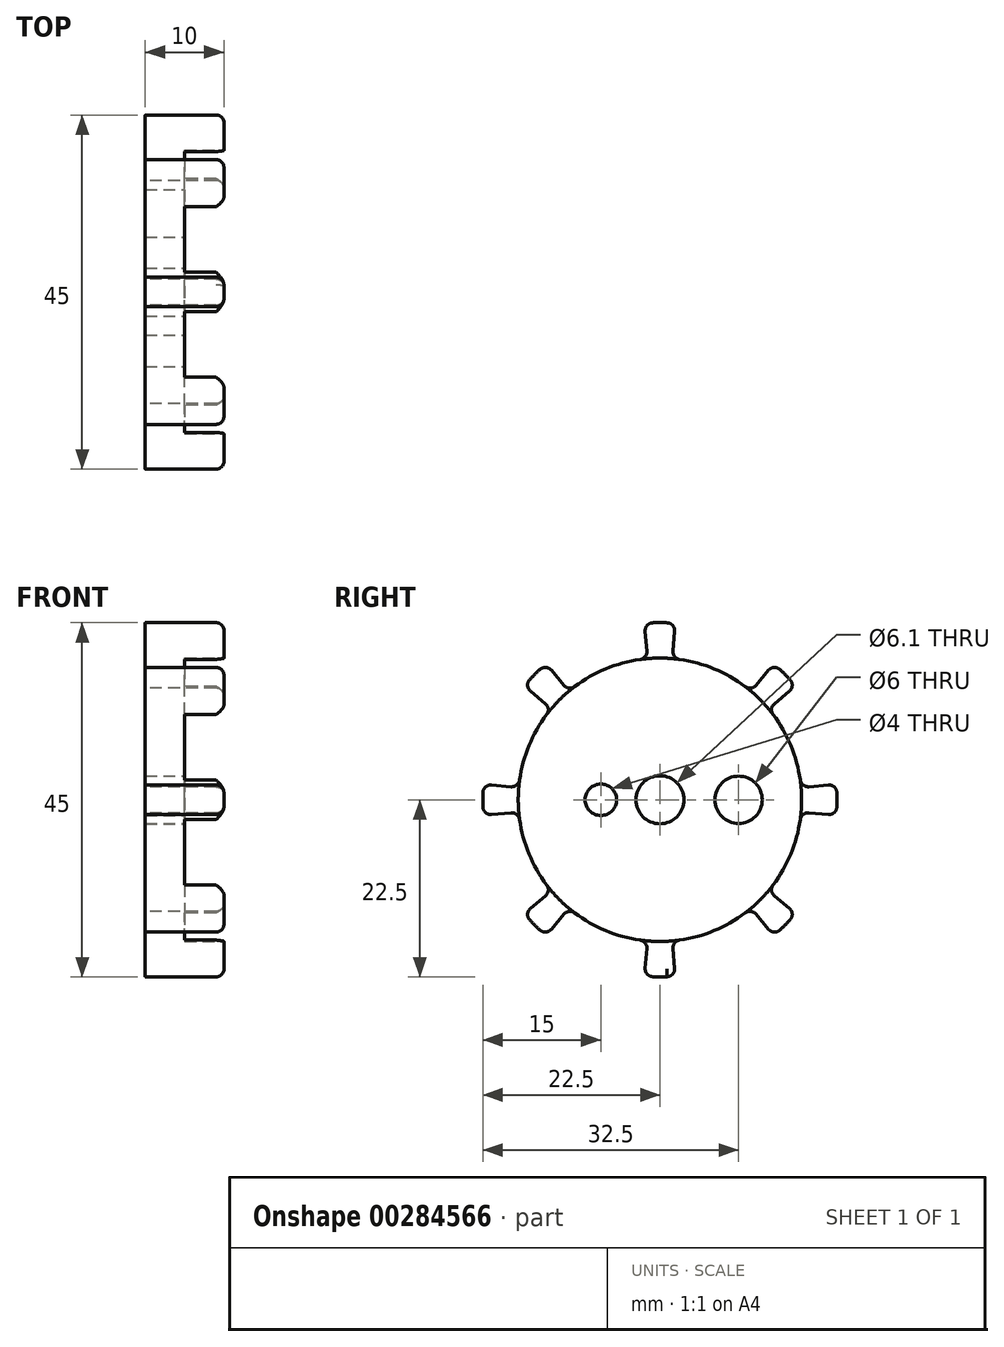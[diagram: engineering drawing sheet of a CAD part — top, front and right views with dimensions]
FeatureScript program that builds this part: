
annotation { "Feature Type Name" : "Feature", "Feature Type Description" : "" }
export const myFeature = defineFeature(function(context is Context, id is Id, definition is map)
    precondition{}
    {
        {
            var Q0;
            Q0=qCreatedBy(makeId("Right.planeOp"),FACE);
            var sketch = newSketch(context, id + "F0", { "sketchPlane" : qUnion([Q0])});
            skArc(sketch, "E0", {"start": v(0.92, 22.48) * mm, "mid": v(0, 22.5) * mm, "end": v(-0.92, 22.48) * mm});
            skArc(sketch, "E1", {"start": v(-2.51, 17.82) * mm, "mid": v(-6.89, 16.63) * mm, "end": v(-10.83, 14.38) * mm});
            skLineSegment(sketch, "E2", {"start": v(0, 22.5) * mm, "end": v(0, 0) * mm, "construction": true});
            skLineSegment(sketch, "E3", {"start": v(1.57, 17.93) * mm, "end": v(0, 0) * mm, "construction": true});
            skLineSegment(sketch, "E4", {"start": v(-1.57, 17.93) * mm, "end": v(0, 0) * mm, "construction": true});
            skLineSegment(sketch, "E5", {"start": v(-1.87, 21.4) * mm, "end": v(-1.65, 18.9) * mm});
            skLineSegment(sketch, "E6", {"start": v(1.87, 21.4) * mm, "end": v(1.65, 18.9) * mm});
            skLineSegment(sketch, "E7.1.0", {"start": v(-16.45, 13.8) * mm, "end": v(-14.53, 12.2) * mm});
            skArc(sketch, "E7.1.1", {"start": v(-15.25, 16.54) * mm, "mid": v(-15.9, 15.9) * mm, "end": v(-16.54, 15.25) * mm});
            skLineSegment(sketch, "E7.1.2", {"start": v(-13.8, 16.45) * mm, "end": v(-12.2, 14.53) * mm});
            skLineSegment(sketch, "E7.2.0", {"start": v(-21.4, -1.87) * mm, "end": v(-18.9, -1.65) * mm});
            skArc(sketch, "E7.2.1", {"start": v(-22.48, 0.92) * mm, "mid": v(-22.5, 0) * mm, "end": v(-22.48, -0.92) * mm});
            skLineSegment(sketch, "E7.2.2", {"start": v(-21.4, 1.87) * mm, "end": v(-18.9, 1.65) * mm});
            skLineSegment(sketch, "E7.3.0", {"start": v(-13.8, -16.45) * mm, "end": v(-12.2, -14.53) * mm});
            skArc(sketch, "E7.3.1", {"start": v(-16.54, -15.25) * mm, "mid": v(-15.9, -15.9) * mm, "end": v(-15.25, -16.54) * mm});
            skLineSegment(sketch, "E7.3.2", {"start": v(-16.45, -13.8) * mm, "end": v(-14.53, -12.2) * mm});
            skLineSegment(sketch, "E7.4.0", {"start": v(1.87, -21.4) * mm, "end": v(1.65, -18.9) * mm});
            skArc(sketch, "E7.4.1", {"start": v(-0.92, -22.48) * mm, "mid": v(0, -22.5) * mm, "end": v(0.92, -22.48) * mm});
            skLineSegment(sketch, "E7.4.2", {"start": v(-1.87, -21.4) * mm, "end": v(-1.65, -18.9) * mm});
            skLineSegment(sketch, "E7.5.0", {"start": v(16.45, -13.8) * mm, "end": v(14.53, -12.2) * mm});
            skArc(sketch, "E7.5.1", {"start": v(15.25, -16.54) * mm, "mid": v(15.9, -15.9) * mm, "end": v(16.54, -15.25) * mm});
            skLineSegment(sketch, "E7.5.2", {"start": v(13.8, -16.45) * mm, "end": v(12.2, -14.53) * mm});
            skLineSegment(sketch, "E7.6.0", {"start": v(21.4, 1.87) * mm, "end": v(18.9, 1.65) * mm});
            skArc(sketch, "E7.6.1", {"start": v(22.48, -0.92) * mm, "mid": v(22.5, 0) * mm, "end": v(22.48, 0.92) * mm});
            skLineSegment(sketch, "E7.6.2", {"start": v(21.4, -1.87) * mm, "end": v(18.9, -1.65) * mm});
            skLineSegment(sketch, "E7.7.0", {"start": v(13.8, 16.45) * mm, "end": v(12.2, 14.53) * mm});
            skArc(sketch, "E7.7.1", {"start": v(16.54, 15.25) * mm, "mid": v(15.9, 15.9) * mm, "end": v(15.25, 16.54) * mm});
            skLineSegment(sketch, "E7.7.2", {"start": v(16.45, 13.8) * mm, "end": v(14.53, 12.2) * mm});
            skArc(sketch, "E8.trimOffspring", {"start": v(-14.38, 10.83) * mm, "mid": v(-16.63, 6.89) * mm, "end": v(-17.82, 2.51) * mm});
            skArc(sketch, "E9.trimOffspring", {"start": v(-17.82, -2.51) * mm, "mid": v(-16.63, -6.89) * mm, "end": v(-14.38, -10.83) * mm});
            skArc(sketch, "E10.trimOffspring", {"start": v(-10.83, -14.38) * mm, "mid": v(-6.89, -16.63) * mm, "end": v(-2.51, -17.82) * mm});
            skArc(sketch, "E11.trimOffspring", {"start": v(2.51, -17.82) * mm, "mid": v(6.89, -16.63) * mm, "end": v(10.83, -14.38) * mm});
            skArc(sketch, "E12.trimOffspring", {"start": v(14.38, -10.83) * mm, "mid": v(16.63, -6.89) * mm, "end": v(17.82, -2.51) * mm});
            skArc(sketch, "E13.trimOffspring", {"start": v(17.82, 2.51) * mm, "mid": v(16.63, 6.89) * mm, "end": v(14.38, 10.83) * mm});
            skArc(sketch, "E14.trimOffspring", {"start": v(10.83, 14.38) * mm, "mid": v(6.89, 16.63) * mm, "end": v(2.51, 17.82) * mm});
            skPoint(sketch, "E15.visualSharp", {"position": v(-1.57, 17.93) * mm});
            skArc(sketch, "E15.filletArc", {"start": v(-2.51, 17.82) * mm, "mid": v(-1.87, 18.2) * mm, "end": v(-1.65, 18.9) * mm});
            skPoint(sketch, "E16.visualSharp", {"position": v(1.57, 17.93) * mm});
            skArc(sketch, "E16.filletArc", {"start": v(1.65, 18.9) * mm, "mid": v(1.87, 18.2) * mm, "end": v(2.51, 17.82) * mm});
            skPoint(sketch, "E17.visualSharp", {"position": v(1.96, 22.41) * mm});
            skArc(sketch, "E17.filletArc", {"start": v(1.87, 21.4) * mm, "mid": v(1.63, 22.14) * mm, "end": v(0.92, 22.48) * mm});
            skPoint(sketch, "E18.visualSharp", {"position": v(-1.96, 22.41) * mm});
            skArc(sketch, "E18.filletArc", {"start": v(-0.92, 22.48) * mm, "mid": v(-1.63, 22.14) * mm, "end": v(-1.87, 21.4) * mm});
            skPoint(sketch, "E19.visualSharp", {"position": v(14.46, 17.24) * mm});
            skArc(sketch, "E19.filletArc", {"start": v(15.25, 16.54) * mm, "mid": v(14.5, 16.8) * mm, "end": v(13.8, 16.45) * mm});
            skPoint(sketch, "E20.visualSharp", {"position": v(11.57, 13.79) * mm});
            skArc(sketch, "E20.filletArc", {"start": v(10.83, 14.38) * mm, "mid": v(11.54, 14.18) * mm, "end": v(12.2, 14.53) * mm});
            skPoint(sketch, "E21.visualSharp", {"position": v(17.24, 14.46) * mm});
            skArc(sketch, "E21.filletArc", {"start": v(16.45, 13.8) * mm, "mid": v(16.8, 14.5) * mm, "end": v(16.54, 15.25) * mm});
            skPoint(sketch, "E22.visualSharp", {"position": v(13.79, 11.57) * mm});
            skArc(sketch, "E22.filletArc", {"start": v(14.53, 12.2) * mm, "mid": v(14.18, 11.54) * mm, "end": v(14.38, 10.83) * mm});
            skPoint(sketch, "E23.visualSharp", {"position": v(17.93, 1.57) * mm});
            skArc(sketch, "E23.filletArc", {"start": v(17.82, 2.51) * mm, "mid": v(18.2, 1.87) * mm, "end": v(18.9, 1.65) * mm});
            skPoint(sketch, "E24.visualSharp", {"position": v(22.41, 1.96) * mm});
            skArc(sketch, "E24.filletArc", {"start": v(22.48, 0.92) * mm, "mid": v(22.14, 1.63) * mm, "end": v(21.4, 1.87) * mm});
            skPoint(sketch, "E25.visualSharp", {"position": v(22.41, -1.96) * mm});
            skArc(sketch, "E25.filletArc", {"start": v(21.4, -1.87) * mm, "mid": v(22.14, -1.63) * mm, "end": v(22.48, -0.92) * mm});
            skPoint(sketch, "E26.visualSharp", {"position": v(17.93, -1.57) * mm});
            skArc(sketch, "E26.filletArc", {"start": v(18.9, -1.65) * mm, "mid": v(18.2, -1.87) * mm, "end": v(17.82, -2.51) * mm});
            skPoint(sketch, "E27.visualSharp", {"position": v(-11.57, 13.79) * mm});
            skArc(sketch, "E27.filletArc", {"start": v(-12.2, 14.53) * mm, "mid": v(-11.54, 14.18) * mm, "end": v(-10.83, 14.38) * mm});
            skPoint(sketch, "E28.visualSharp", {"position": v(-14.46, 17.24) * mm});
            skArc(sketch, "E28.filletArc", {"start": v(-13.8, 16.45) * mm, "mid": v(-14.5, 16.8) * mm, "end": v(-15.25, 16.54) * mm});
            skPoint(sketch, "E29.visualSharp", {"position": v(-17.24, 14.46) * mm});
            skArc(sketch, "E29.filletArc", {"start": v(-16.54, 15.25) * mm, "mid": v(-16.8, 14.5) * mm, "end": v(-16.45, 13.8) * mm});
            skPoint(sketch, "E30.visualSharp", {"position": v(-13.79, 11.57) * mm});
            skArc(sketch, "E30.filletArc", {"start": v(-14.38, 10.83) * mm, "mid": v(-14.18, 11.54) * mm, "end": v(-14.53, 12.2) * mm});
            skPoint(sketch, "E31.visualSharp", {"position": v(-17.93, 1.57) * mm});
            skArc(sketch, "E31.filletArc", {"start": v(-18.9, 1.65) * mm, "mid": v(-18.2, 1.87) * mm, "end": v(-17.82, 2.51) * mm});
            skPoint(sketch, "E32.visualSharp", {"position": v(-22.41, 1.96) * mm});
            skArc(sketch, "E32.filletArc", {"start": v(-21.4, 1.87) * mm, "mid": v(-22.14, 1.63) * mm, "end": v(-22.48, 0.92) * mm});
            skPoint(sketch, "E33.visualSharp", {"position": v(-22.41, -1.96) * mm});
            skArc(sketch, "E33.filletArc", {"start": v(-22.48, -0.92) * mm, "mid": v(-22.14, -1.63) * mm, "end": v(-21.4, -1.87) * mm});
            skPoint(sketch, "E34.visualSharp", {"position": v(-17.93, -1.57) * mm});
            skArc(sketch, "E34.filletArc", {"start": v(-17.82, -2.51) * mm, "mid": v(-18.2, -1.87) * mm, "end": v(-18.9, -1.65) * mm});
            skPoint(sketch, "E35.visualSharp", {"position": v(-13.79, -11.57) * mm});
            skArc(sketch, "E35.filletArc", {"start": v(-14.53, -12.2) * mm, "mid": v(-14.18, -11.54) * mm, "end": v(-14.38, -10.83) * mm});
            skPoint(sketch, "E36.visualSharp", {"position": v(-17.24, -14.46) * mm});
            skArc(sketch, "E36.filletArc", {"start": v(-16.45, -13.8) * mm, "mid": v(-16.8, -14.5) * mm, "end": v(-16.54, -15.25) * mm});
            skPoint(sketch, "E37.visualSharp", {"position": v(-14.46, -17.24) * mm});
            skArc(sketch, "E37.filletArc", {"start": v(-15.25, -16.54) * mm, "mid": v(-14.5, -16.8) * mm, "end": v(-13.8, -16.45) * mm});
            skPoint(sketch, "E38.visualSharp", {"position": v(-11.57, -13.79) * mm});
            skArc(sketch, "E38.filletArc", {"start": v(-10.83, -14.38) * mm, "mid": v(-11.54, -14.18) * mm, "end": v(-12.2, -14.53) * mm});
            skPoint(sketch, "E39.visualSharp", {"position": v(-1.57, -17.93) * mm});
            skArc(sketch, "E39.filletArc", {"start": v(-1.65, -18.9) * mm, "mid": v(-1.87, -18.2) * mm, "end": v(-2.51, -17.82) * mm});
            skPoint(sketch, "E40.visualSharp", {"position": v(-1.96, -22.41) * mm});
            skArc(sketch, "E40.filletArc", {"start": v(-1.87, -21.4) * mm, "mid": v(-1.63, -22.14) * mm, "end": v(-0.92, -22.48) * mm});
            skPoint(sketch, "E41.visualSharp", {"position": v(1.96, -22.41) * mm});
            skArc(sketch, "E41.filletArc", {"start": v(0.92, -22.48) * mm, "mid": v(1.63, -22.14) * mm, "end": v(1.87, -21.4) * mm});
            skPoint(sketch, "E42.visualSharp", {"position": v(1.57, -17.93) * mm});
            skArc(sketch, "E42.filletArc", {"start": v(2.51, -17.82) * mm, "mid": v(1.87, -18.2) * mm, "end": v(1.65, -18.9) * mm});
            skPoint(sketch, "E43.visualSharp", {"position": v(11.57, -13.79) * mm});
            skArc(sketch, "E43.filletArc", {"start": v(12.2, -14.53) * mm, "mid": v(11.54, -14.18) * mm, "end": v(10.83, -14.38) * mm});
            skPoint(sketch, "E44.visualSharp", {"position": v(14.46, -17.24) * mm});
            skArc(sketch, "E44.filletArc", {"start": v(13.8, -16.45) * mm, "mid": v(14.5, -16.8) * mm, "end": v(15.25, -16.54) * mm});
            skPoint(sketch, "E45.visualSharp", {"position": v(17.24, -14.46) * mm});
            skArc(sketch, "E45.filletArc", {"start": v(16.54, -15.25) * mm, "mid": v(16.8, -14.5) * mm, "end": v(16.45, -13.8) * mm});
            skPoint(sketch, "E46.visualSharp", {"position": v(13.79, -11.57) * mm});
            skArc(sketch, "E46.filletArc", {"start": v(14.38, -10.83) * mm, "mid": v(14.18, -11.54) * mm, "end": v(14.53, -12.2) * mm});
            skSolve(sketch);
        }
        {
            var Q0;
            Q0=qSketchRegion(id+"F0",true);
            extrude(context, id + "F1", {"entities" : qUnion([Q0]), "depth" : 10 * mm});
        }
        {
            var Q0;
            Q0=makeQuery(id+"F1.opExtrude","CAP_FACE",FACE,{"disambiguationData":[OSD([sQuery(id+"F0.wireOp",EDGE,"E0"),sQuery(id+"F0.wireOp",EDGE,"E1"),sQuery(id+"F0.wireOp",EDGE,"E5"),sQuery(id+"F0.wireOp",EDGE,"E6"),sQuery(id+"F0.wireOp",EDGE,"E7.1.0"),sQuery(id+"F0.wireOp",EDGE,"E7.1.1"),sQuery(id+"F0.wireOp",EDGE,"E7.1.2"),sQuery(id+"F0.wireOp",EDGE,"E7.2.0"),sQuery(id+"F0.wireOp",EDGE,"E7.2.1"),sQuery(id+"F0.wireOp",EDGE,"E7.2.2"),sQuery(id+"F0.wireOp",EDGE,"E7.3.0"),sQuery(id+"F0.wireOp",EDGE,"E7.3.1"),sQuery(id+"F0.wireOp",EDGE,"E7.3.2"),sQuery(id+"F0.wireOp",EDGE,"E7.4.0"),sQuery(id+"F0.wireOp",EDGE,"E7.4.1"),sQuery(id+"F0.wireOp",EDGE,"E7.4.2"),sQuery(id+"F0.wireOp",EDGE,"E7.5.0"),sQuery(id+"F0.wireOp",EDGE,"E7.5.1"),sQuery(id+"F0.wireOp",EDGE,"E7.5.2"),sQuery(id+"F0.wireOp",EDGE,"E7.6.0"),sQuery(id+"F0.wireOp",EDGE,"E7.6.1"),sQuery(id+"F0.wireOp",EDGE,"E7.6.2"),sQuery(id+"F0.wireOp",EDGE,"E7.7.0"),sQuery(id+"F0.wireOp",EDGE,"E7.7.1"),sQuery(id+"F0.wireOp",EDGE,"E7.7.2"),sQuery(id+"F0.wireOp",EDGE,"E8.trimOffspring"),sQuery(id+"F0.wireOp",EDGE,"E9.trimOffspring"),sQuery(id+"F0.wireOp",EDGE,"E10.trimOffspring"),sQuery(id+"F0.wireOp",EDGE,"E11.trimOffspring"),sQuery(id+"F0.wireOp",EDGE,"E12.trimOffspring"),sQuery(id+"F0.wireOp",EDGE,"E13.trimOffspring"),sQuery(id+"F0.wireOp",EDGE,"E14.trimOffspring")])],"isStart":false});
            var sketch = newSketch(context, id + "F2", { "sketchPlane" : qUnion([Q0])});
            skCircle(sketch, "E47", {"center": v(0, 0) * mm, "radius": 18 * mm});
            skSolve(sketch);
        }
        {
            var Q0;
            Q0=qSketchRegion(id+"F2",true);
            extrude(context, id + "F3", {"entities" : qUnion([Q0]), "operationType" : NewBodyOperationType.REMOVE, "oppositeDirection" : true, "depth" : 5 * mm});
        }
        {
            var Q0;
            Q0=makeQuery(id+"F3.boolean.opBoolean","COPY",FACE,{"derivedFrom":makeQuery(id+"F3.opExtrude","CAP_FACE",FACE,{"disambiguationData":[OSD([sQuery(id+"F2.wireOp",EDGE,"E47")])],"isStart":false})});
            var sketch = newSketch(context, id + "F4", { "sketchPlane" : qUnion([Q0])});
            skPoint(sketch, "E48", {"position": v(10, 0) * mm});
            skPoint(sketch, "E49", {"position": v(0, 0) * mm});
            skPoint(sketch, "E50", {"position": v(-7.5, 0) * mm});
            skSolve(sketch);
        }
        {
            var Q0;
            Q0=sQuery(id+"F4.wireOp",VERTEX,"E49");
            var Q1;
            Q1=makeQuery(id+"F1.opExtrude","SWEPT_BODY",BODY,{"disambiguationData":[OSD([sQuery(id+"F0.wireOp",EDGE,"E0"),sQuery(id+"F0.wireOp",EDGE,"E1"),sQuery(id+"F0.wireOp",EDGE,"E5"),sQuery(id+"F0.wireOp",EDGE,"E6"),sQuery(id+"F0.wireOp",EDGE,"E7.1.0"),sQuery(id+"F0.wireOp",EDGE,"E7.1.1"),sQuery(id+"F0.wireOp",EDGE,"E7.1.2"),sQuery(id+"F0.wireOp",EDGE,"E7.2.0"),sQuery(id+"F0.wireOp",EDGE,"E7.2.1"),sQuery(id+"F0.wireOp",EDGE,"E7.2.2"),sQuery(id+"F0.wireOp",EDGE,"E7.3.0"),sQuery(id+"F0.wireOp",EDGE,"E7.3.1"),sQuery(id+"F0.wireOp",EDGE,"E7.3.2"),sQuery(id+"F0.wireOp",EDGE,"E7.4.0"),sQuery(id+"F0.wireOp",EDGE,"E7.4.1"),sQuery(id+"F0.wireOp",EDGE,"E7.4.2"),sQuery(id+"F0.wireOp",EDGE,"E7.5.0"),sQuery(id+"F0.wireOp",EDGE,"E7.5.1"),sQuery(id+"F0.wireOp",EDGE,"E7.5.2"),sQuery(id+"F0.wireOp",EDGE,"E7.6.0"),sQuery(id+"F0.wireOp",EDGE,"E7.6.1"),sQuery(id+"F0.wireOp",EDGE,"E7.6.2"),sQuery(id+"F0.wireOp",EDGE,"E7.7.0"),sQuery(id+"F0.wireOp",EDGE,"E7.7.1"),sQuery(id+"F0.wireOp",EDGE,"E7.7.2"),sQuery(id+"F0.wireOp",EDGE,"E8.trimOffspring"),sQuery(id+"F0.wireOp",EDGE,"E9.trimOffspring"),sQuery(id+"F0.wireOp",EDGE,"E10.trimOffspring"),sQuery(id+"F0.wireOp",EDGE,"E11.trimOffspring"),sQuery(id+"F0.wireOp",EDGE,"E12.trimOffspring"),sQuery(id+"F0.wireOp",EDGE,"E13.trimOffspring"),sQuery(id+"F0.wireOp",EDGE,"E14.trimOffspring"),sQuery(id+"F0.wireOp",EDGE,"E15.filletArc"),sQuery(id+"F0.wireOp",EDGE,"E16.filletArc"),sQuery(id+"F0.wireOp",EDGE,"E17.filletArc"),sQuery(id+"F0.wireOp",EDGE,"E18.filletArc"),sQuery(id+"F0.wireOp",EDGE,"E19.filletArc"),sQuery(id+"F0.wireOp",EDGE,"E20.filletArc"),sQuery(id+"F0.wireOp",EDGE,"E21.filletArc"),sQuery(id+"F0.wireOp",EDGE,"E22.filletArc"),sQuery(id+"F0.wireOp",EDGE,"E23.filletArc"),sQuery(id+"F0.wireOp",EDGE,"E24.filletArc"),sQuery(id+"F0.wireOp",EDGE,"E25.filletArc"),sQuery(id+"F0.wireOp",EDGE,"E26.filletArc"),sQuery(id+"F0.wireOp",EDGE,"E27.filletArc"),sQuery(id+"F0.wireOp",EDGE,"E28.filletArc"),sQuery(id+"F0.wireOp",EDGE,"E29.filletArc"),sQuery(id+"F0.wireOp",EDGE,"E30.filletArc"),sQuery(id+"F0.wireOp",EDGE,"E31.filletArc"),sQuery(id+"F0.wireOp",EDGE,"E32.filletArc"),sQuery(id+"F0.wireOp",EDGE,"E33.filletArc"),sQuery(id+"F0.wireOp",EDGE,"E34.filletArc"),sQuery(id+"F0.wireOp",EDGE,"E35.filletArc"),sQuery(id+"F0.wireOp",EDGE,"E36.filletArc"),sQuery(id+"F0.wireOp",EDGE,"E37.filletArc"),sQuery(id+"F0.wireOp",EDGE,"E38.filletArc"),sQuery(id+"F0.wireOp",EDGE,"E39.filletArc"),sQuery(id+"F0.wireOp",EDGE,"E40.filletArc"),sQuery(id+"F0.wireOp",EDGE,"E41.filletArc"),sQuery(id+"F0.wireOp",EDGE,"E42.filletArc"),sQuery(id+"F0.wireOp",EDGE,"E43.filletArc"),sQuery(id+"F0.wireOp",EDGE,"E44.filletArc"),sQuery(id+"F0.wireOp",EDGE,"E45.filletArc"),sQuery(id+"F0.wireOp",EDGE,"E46.filletArc")])]});
            hole(context, id + "F5", {"style" : HoleStyle.SIMPLE, "endStyle" : HoleEndStyle.THROUGH, "holeDiameter" : 6.1 * mm, "locations" : qUnion([Q0]), "scope" : qUnion([Q1]), "isTappedThrough" : true});
        }
        {
            var Q0;
            Q0=makeQuery(id+"F1.opExtrude","CAP_EDGE",EDGE,{"disambiguationData":[OSD([sQuery(id+"F0.wireOp",EDGE,"E7.1.1")])],"isStart":false});
            var Q1;
            Q1=makeQuery(id+"F1.opExtrude","CAP_EDGE",EDGE,{"disambiguationData":[OSD([sQuery(id+"F0.wireOp",EDGE,"E7.2.1")])],"isStart":false});
            var Q2;
            Q2=makeQuery(id+"F1.opExtrude","CAP_EDGE",EDGE,{"disambiguationData":[OSD([sQuery(id+"F0.wireOp",EDGE,"E7.3.1")])],"isStart":false});
            var Q3;
            Q3=makeQuery(id+"F1.opExtrude","CAP_EDGE",EDGE,{"disambiguationData":[OSD([sQuery(id+"F0.wireOp",EDGE,"E7.4.1")])],"isStart":false});
            var Q4;
            Q4=makeQuery(id+"F1.opExtrude","CAP_EDGE",EDGE,{"disambiguationData":[OSD([sQuery(id+"F0.wireOp",EDGE,"E7.5.1")])],"isStart":false});
            var Q5;
            Q5=makeQuery(id+"F1.opExtrude","CAP_EDGE",EDGE,{"disambiguationData":[OSD([sQuery(id+"F0.wireOp",EDGE,"E7.6.1")])],"isStart":false});
            var Q6;
            Q6=makeQuery(id+"F1.opExtrude","CAP_EDGE",EDGE,{"disambiguationData":[OSD([sQuery(id+"F0.wireOp",EDGE,"E7.7.1")])],"isStart":false});
            var Q7;
            Q7=makeQuery(id+"F1.opExtrude","CAP_EDGE",EDGE,{"disambiguationData":[OSD([sQuery(id+"F0.wireOp",EDGE,"E0")])],"isStart":false});
            fillet(context, id + "F6", {"entities" : qUnion([Q0, Q1, Q2, Q3, Q4, Q5, Q6, Q7]), "radius" : 1 * mm, "tangentPropagation" : true, "allowEdgeOverflow" : false});
        }
        {
            var Q0;
            Q0=sQuery(id+"F4.wireOp",VERTEX,"E48");
            var Q1;
            Q1=makeQuery(id+"F1.opExtrude","SWEPT_BODY",BODY,{"disambiguationData":[OSD([sQuery(id+"F0.wireOp",EDGE,"E0"),sQuery(id+"F0.wireOp",EDGE,"E1"),sQuery(id+"F0.wireOp",EDGE,"E5"),sQuery(id+"F0.wireOp",EDGE,"E6"),sQuery(id+"F0.wireOp",EDGE,"E7.1.0"),sQuery(id+"F0.wireOp",EDGE,"E7.1.1"),sQuery(id+"F0.wireOp",EDGE,"E7.1.2"),sQuery(id+"F0.wireOp",EDGE,"E7.2.0"),sQuery(id+"F0.wireOp",EDGE,"E7.2.1"),sQuery(id+"F0.wireOp",EDGE,"E7.2.2"),sQuery(id+"F0.wireOp",EDGE,"E7.3.0"),sQuery(id+"F0.wireOp",EDGE,"E7.3.1"),sQuery(id+"F0.wireOp",EDGE,"E7.3.2"),sQuery(id+"F0.wireOp",EDGE,"E7.4.0"),sQuery(id+"F0.wireOp",EDGE,"E7.4.1"),sQuery(id+"F0.wireOp",EDGE,"E7.4.2"),sQuery(id+"F0.wireOp",EDGE,"E7.5.0"),sQuery(id+"F0.wireOp",EDGE,"E7.5.1"),sQuery(id+"F0.wireOp",EDGE,"E7.5.2"),sQuery(id+"F0.wireOp",EDGE,"E7.6.0"),sQuery(id+"F0.wireOp",EDGE,"E7.6.1"),sQuery(id+"F0.wireOp",EDGE,"E7.6.2"),sQuery(id+"F0.wireOp",EDGE,"E7.7.0"),sQuery(id+"F0.wireOp",EDGE,"E7.7.1"),sQuery(id+"F0.wireOp",EDGE,"E7.7.2"),sQuery(id+"F0.wireOp",EDGE,"E8.trimOffspring"),sQuery(id+"F0.wireOp",EDGE,"E9.trimOffspring"),sQuery(id+"F0.wireOp",EDGE,"E10.trimOffspring"),sQuery(id+"F0.wireOp",EDGE,"E11.trimOffspring"),sQuery(id+"F0.wireOp",EDGE,"E12.trimOffspring"),sQuery(id+"F0.wireOp",EDGE,"E13.trimOffspring"),sQuery(id+"F0.wireOp",EDGE,"E14.trimOffspring"),sQuery(id+"F0.wireOp",EDGE,"E15.filletArc"),sQuery(id+"F0.wireOp",EDGE,"E16.filletArc"),sQuery(id+"F0.wireOp",EDGE,"E17.filletArc"),sQuery(id+"F0.wireOp",EDGE,"E18.filletArc"),sQuery(id+"F0.wireOp",EDGE,"E19.filletArc"),sQuery(id+"F0.wireOp",EDGE,"E20.filletArc"),sQuery(id+"F0.wireOp",EDGE,"E21.filletArc"),sQuery(id+"F0.wireOp",EDGE,"E22.filletArc"),sQuery(id+"F0.wireOp",EDGE,"E23.filletArc"),sQuery(id+"F0.wireOp",EDGE,"E24.filletArc"),sQuery(id+"F0.wireOp",EDGE,"E25.filletArc"),sQuery(id+"F0.wireOp",EDGE,"E26.filletArc"),sQuery(id+"F0.wireOp",EDGE,"E27.filletArc"),sQuery(id+"F0.wireOp",EDGE,"E28.filletArc"),sQuery(id+"F0.wireOp",EDGE,"E29.filletArc"),sQuery(id+"F0.wireOp",EDGE,"E30.filletArc"),sQuery(id+"F0.wireOp",EDGE,"E31.filletArc"),sQuery(id+"F0.wireOp",EDGE,"E32.filletArc"),sQuery(id+"F0.wireOp",EDGE,"E33.filletArc"),sQuery(id+"F0.wireOp",EDGE,"E34.filletArc"),sQuery(id+"F0.wireOp",EDGE,"E35.filletArc"),sQuery(id+"F0.wireOp",EDGE,"E36.filletArc"),sQuery(id+"F0.wireOp",EDGE,"E37.filletArc"),sQuery(id+"F0.wireOp",EDGE,"E38.filletArc"),sQuery(id+"F0.wireOp",EDGE,"E39.filletArc"),sQuery(id+"F0.wireOp",EDGE,"E40.filletArc"),sQuery(id+"F0.wireOp",EDGE,"E41.filletArc"),sQuery(id+"F0.wireOp",EDGE,"E42.filletArc"),sQuery(id+"F0.wireOp",EDGE,"E43.filletArc"),sQuery(id+"F0.wireOp",EDGE,"E44.filletArc"),sQuery(id+"F0.wireOp",EDGE,"E45.filletArc"),sQuery(id+"F0.wireOp",EDGE,"E46.filletArc")])]});
            hole(context, id + "F7", {"style" : HoleStyle.SIMPLE, "endStyle" : HoleEndStyle.THROUGH, "holeDiameter" : 6 * mm, "locations" : qUnion([Q0]), "scope" : qUnion([Q1]), "isTappedThrough" : true});
        }
        {
            var Q0;
            Q0=sQuery(id+"F4.wireOp",VERTEX,"E50");
            var Q1;
            Q1=makeQuery(id+"F1.opExtrude","SWEPT_BODY",BODY,{"disambiguationData":[OSD([sQuery(id+"F0.wireOp",EDGE,"E0"),sQuery(id+"F0.wireOp",EDGE,"E1"),sQuery(id+"F0.wireOp",EDGE,"E5"),sQuery(id+"F0.wireOp",EDGE,"E6"),sQuery(id+"F0.wireOp",EDGE,"E7.1.0"),sQuery(id+"F0.wireOp",EDGE,"E7.1.1"),sQuery(id+"F0.wireOp",EDGE,"E7.1.2"),sQuery(id+"F0.wireOp",EDGE,"E7.2.0"),sQuery(id+"F0.wireOp",EDGE,"E7.2.1"),sQuery(id+"F0.wireOp",EDGE,"E7.2.2"),sQuery(id+"F0.wireOp",EDGE,"E7.3.0"),sQuery(id+"F0.wireOp",EDGE,"E7.3.1"),sQuery(id+"F0.wireOp",EDGE,"E7.3.2"),sQuery(id+"F0.wireOp",EDGE,"E7.4.0"),sQuery(id+"F0.wireOp",EDGE,"E7.4.1"),sQuery(id+"F0.wireOp",EDGE,"E7.4.2"),sQuery(id+"F0.wireOp",EDGE,"E7.5.0"),sQuery(id+"F0.wireOp",EDGE,"E7.5.1"),sQuery(id+"F0.wireOp",EDGE,"E7.5.2"),sQuery(id+"F0.wireOp",EDGE,"E7.6.0"),sQuery(id+"F0.wireOp",EDGE,"E7.6.1"),sQuery(id+"F0.wireOp",EDGE,"E7.6.2"),sQuery(id+"F0.wireOp",EDGE,"E7.7.0"),sQuery(id+"F0.wireOp",EDGE,"E7.7.1"),sQuery(id+"F0.wireOp",EDGE,"E7.7.2"),sQuery(id+"F0.wireOp",EDGE,"E8.trimOffspring"),sQuery(id+"F0.wireOp",EDGE,"E9.trimOffspring"),sQuery(id+"F0.wireOp",EDGE,"E10.trimOffspring"),sQuery(id+"F0.wireOp",EDGE,"E11.trimOffspring"),sQuery(id+"F0.wireOp",EDGE,"E12.trimOffspring"),sQuery(id+"F0.wireOp",EDGE,"E13.trimOffspring"),sQuery(id+"F0.wireOp",EDGE,"E14.trimOffspring"),sQuery(id+"F0.wireOp",EDGE,"E15.filletArc"),sQuery(id+"F0.wireOp",EDGE,"E16.filletArc"),sQuery(id+"F0.wireOp",EDGE,"E17.filletArc"),sQuery(id+"F0.wireOp",EDGE,"E18.filletArc"),sQuery(id+"F0.wireOp",EDGE,"E19.filletArc"),sQuery(id+"F0.wireOp",EDGE,"E20.filletArc"),sQuery(id+"F0.wireOp",EDGE,"E21.filletArc"),sQuery(id+"F0.wireOp",EDGE,"E22.filletArc"),sQuery(id+"F0.wireOp",EDGE,"E23.filletArc"),sQuery(id+"F0.wireOp",EDGE,"E24.filletArc"),sQuery(id+"F0.wireOp",EDGE,"E25.filletArc"),sQuery(id+"F0.wireOp",EDGE,"E26.filletArc"),sQuery(id+"F0.wireOp",EDGE,"E27.filletArc"),sQuery(id+"F0.wireOp",EDGE,"E28.filletArc"),sQuery(id+"F0.wireOp",EDGE,"E29.filletArc"),sQuery(id+"F0.wireOp",EDGE,"E30.filletArc"),sQuery(id+"F0.wireOp",EDGE,"E31.filletArc"),sQuery(id+"F0.wireOp",EDGE,"E32.filletArc"),sQuery(id+"F0.wireOp",EDGE,"E33.filletArc"),sQuery(id+"F0.wireOp",EDGE,"E34.filletArc"),sQuery(id+"F0.wireOp",EDGE,"E35.filletArc"),sQuery(id+"F0.wireOp",EDGE,"E36.filletArc"),sQuery(id+"F0.wireOp",EDGE,"E37.filletArc"),sQuery(id+"F0.wireOp",EDGE,"E38.filletArc"),sQuery(id+"F0.wireOp",EDGE,"E39.filletArc"),sQuery(id+"F0.wireOp",EDGE,"E40.filletArc"),sQuery(id+"F0.wireOp",EDGE,"E41.filletArc"),sQuery(id+"F0.wireOp",EDGE,"E42.filletArc"),sQuery(id+"F0.wireOp",EDGE,"E43.filletArc"),sQuery(id+"F0.wireOp",EDGE,"E44.filletArc"),sQuery(id+"F0.wireOp",EDGE,"E45.filletArc"),sQuery(id+"F0.wireOp",EDGE,"E46.filletArc")])]});
            hole(context, id + "F8", {"style" : HoleStyle.SIMPLE, "endStyle" : HoleEndStyle.THROUGH, "holeDiameter" : 4 * mm, "locations" : qUnion([Q0]), "scope" : qUnion([Q1]), "isTappedThrough" : true});
        }
    });
